# Revit family: xBathtub-American_Standard-New_Solar_AFR-0263_Series
name_source: partatom
category: Plumbing Fixtures
units: mm (PartAtom-declared; Revit-internal decimal feet)

## family parameters
Always vertical = No
Cut with Voids When Loaded = No
OmniClass Number = 23.45.05.14.21
OmniClass Title = Bathtubs
Part Type = Normal
Room Calculation Point = No
Round Connector Dimension = Use Diameter
Shared = Yes
Work Plane-Based = Yes

## types (2) — shared parameters
ADA Compliant = Yes
ASME A112.19.4 for Enameled Steel Plumbing = Yes
ASTM F-462 for Slip-resistant Bathing Facilities = Yes
Assembly Code = D2010510
Bath Type = Bathing Pool
Bathing Well Depth = 13 1/4"
CW Connection = No
CWFU = 3
Default Elevation = 0"
Finish = Enameled Steel-American Standard-020-White
HW Connection = No
HWFU = 3
Height = 16 5/8"
Length = 30"
Lumbar Support = Fully-Bonded Support Pad
Manufacturer = American Standard
Material = Enameled Steel-American Standard-020-White
Product Documentation Link = https://americanstandard.box.com
Product Page URL = https://www.americanstandard-us.com
Product Style = Integral Apron
Revised Date = 10/08/2021
Shipping Weight = 85lbs. (39 kg)
Tiling Flange Height = 13/16"
Tub Type = Alcove Rectangular Bath Tub
URL = https://www.americanstandard-us.com
Vent Connection = No
WFU = 4
Waste Connection = Yes
Waste Connection Diameter = 2 1/8"
Waste Outlet Offset = 14 3/8"
Water Retention Flange = Straight Tiling Flange
Width = 60"

## per-type parameters (varying)
| type | Description | Left-Hand Outlet | Outlet Location | Right-Hand Outlet |
| 0263.112.020 | New Solar® 60 x 30-Inch Integral Apron Bathtub Above Floor Rough With Right-Hand Outlet | No | 52" | Yes |
| 0263.212.020 | New Solar® 60 x 30-Inch Integral Apron Bathtub Above Floor Rough With Left-Hand Outlet | Yes | 8" | No |

note: column(s) folded — value = type name in every type: Model

## geometry (parser evidence)
native form markers: Sweep x2
no freeform markers — native parametric forms only
